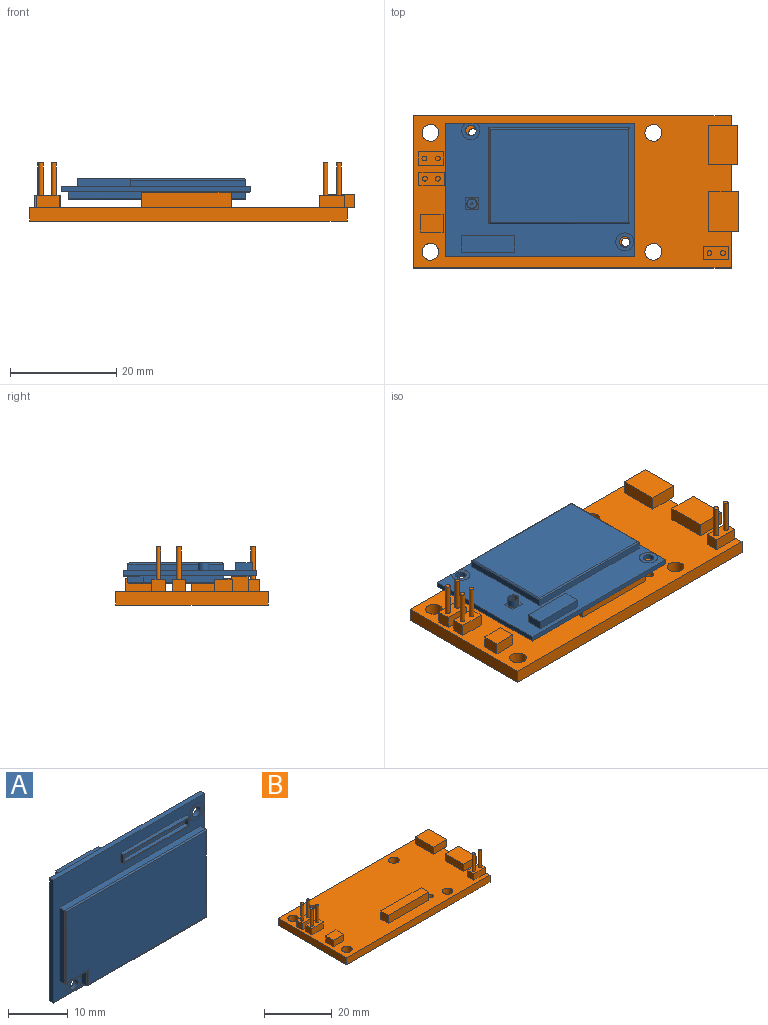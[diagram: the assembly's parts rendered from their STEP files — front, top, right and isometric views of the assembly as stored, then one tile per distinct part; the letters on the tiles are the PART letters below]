
ASSEMBLY  parts=2 mates=1
PART A: 64 faces, bbox 35.6x4x25.1 mm
  f0: plane 35.56x25.08mm, normal (0,1,0), area 359.8mm2, adj f2,f3,f4,f5,f6,f7,f8,f9
  f1: plane 35.56x25.08mm, normal (0,-1,0), area 260mm2, adj f2,f3,f4,f5,f11,f12,f13,f14
  f2: plane 25.08x0.95mm, normal (1,0,0), area 23.8mm2, adj f0,f1,f3,f5
  f3: plane 35.56x0.96mm, normal (0,0,-1), area 33.8mm2, adj f0,f1,f2,f4,f37,f38,f39,f40
  f4: plane 25.08x0.95mm, normal (-1,0,0), area 23.8mm2, adj f0,f1,f3,f5
  f5: plane 35.56x0.95mm, normal (0,0,1), area 33.8mm2, adj f0,f1,f2,f4
  f6: plane 18x1.25mm, normal (-1,0,0), area 22.5mm2, adj f0,f7,f9,f51
  f7: plane 26.5x1.25mm, normal (0,0,1), area 33.1mm2, adj f0,f6,f8,f49
  f8: plane 18x1.25mm, normal (1,0,0), area 22.5mm2, adj f0,f7,f9,f50
  f9: plane 26.5x1.25mm, normal (0,0,-1), area 33.1mm2, adj f0,f6,f8,f52
  f10: plane 26x17.5mm, normal (0,1,0), area 455mm2, adj f49,f50,f51,f52
  f11: plane 28.15x1.25mm, normal (0,0,-1), area 35.2mm2, adj f1,f12,f16,f47
  f12: plane 18x1.25mm, normal (1,0,0), area 22.5mm2, adj f1,f11,f13,f45
  f13: plane 33.4x1.25mm, normal (0,0,1), area 41.7mm2, adj f1,f12,f14,f43
  f14: plane 15x1.25mm, normal (-1,0,0), area 18.8mm2, adj f1,f13,f15,f44
  f15: plane 5.25x1.25mm, normal (0,0,-1), area 6.6mm2, adj f1,f14,f16,f46
  f16: plane 3x1.25mm, normal (-1,0,0), area 3.8mm2, adj f1,f11,f15,f48
  f17: plane 32.9x17.5mm, normal (0,-1,0), area 560mm2, adj f43,f44,f45,f46,f47,f48
  f18: plane 10x1.56mm, normal (0,0,-1), area 15.6mm2, adj f0,f19,f21,f22
  f19: plane 3.18x1.56mm, normal (-1,0,0), area 5mm2, adj f0,f18,f20,f22
  f20: plane 10x1.56mm, normal (0,0,1), area 15.6mm2, adj f0,f19,f21,f22
  f21: plane 3.18x1.56mm, normal (1,0,0), area 5mm2, adj f0,f18,f20,f22
  f22: plane 10x3.18mm, normal (0,1,0), area 31.8mm2, adj f18,f19,f20,f21
  f23: plane 15.5x1.85mm, normal (0,-1,0), area 8.4mm2, adj f24,f25,f26,f27,f28,f29,f30,f31
  f24: plane 15.5x0.75mm, normal (0,0,-1), area 11.6mm2, adj f1,f23,f25,f27
  f25: plane 1.85x0.75mm, normal (1,0,0), area 1.4mm2, adj f1,f23,f24,f26
  f26: plane 15.5x0.75mm, normal (0,0,1), area 11.6mm2, adj f1,f23,f25,f27
  f27: plane 1.85x0.75mm, normal (-1,0,0), area 1.4mm2, adj f1,f23,f24,f26
  f28: plane 1.35x0.75mm, normal (1,0,0), area 1mm2, adj f23,f29,f31,f32
  f29: plane 15x0.75mm, normal (0,0,1), area 11.2mm2, adj f23,f28,f30,f32
  f30: plane 1.35x0.75mm, normal (-1,0,0), area 1mm2, adj f23,f29,f31,f32
  f31: plane 15x0.75mm, normal (0,0,-1), area 11.2mm2, adj f23,f28,f30,f32
  f32: plane 15x1.35mm, normal (0,-1,0), area 20.3mm2, adj f28,f29,f30,f31
  f33: cylinder r=1mm len=2mm, axis (0,-1,0), area 6mm2, adj f35,f42
  f34: cylinder r=1mm len=2mm, axis (0,1,0), area 6mm2, adj f37,f40
  f35: plane 3.4x3.4mm, normal (0,1,0), area 5.9mm2, adj f33,f36
  f36: cylinder r=1.7mm len=3.4mm, axis (0,-1,0), area 0mm2, adj f0,f35
  f37: plane 3.4x3.06mm, normal (0,1,0), area 5.5mm2, adj f3,f34,f38
  f38: cylinder r=1.7mm len=3.4mm, axis (0,-1,0), area 0mm2, adj f0,f3,f37
  f39: cylinder r=1.7mm len=3.4mm, axis (0,-1,0), area 0mm2, adj f1,f3,f40
  f40: plane 3.4x3.06mm, normal (0,-1,0), area 5.5mm2, adj f3,f34,f39
  f41: cylinder r=1.7mm len=3.4mm, axis (0,-1,0), area 0mm2, adj f1,f42
  f42: plane 3.4x3.4mm, normal (0,-1,0), area 5.9mm2, adj f33,f41
  f43: cylinder r=0.25mm len=33.4mm, axis (1,0,0), area 13mm2, adj f13,f17,f44,f45
  f44: cylinder r=0.25mm len=15mm, axis (0,0,1), area 5.8mm2, adj f14,f17,f43,f46
  f45: cylinder r=0.25mm len=18mm, axis (0,0,-1), area 7mm2, adj f12,f17,f43,f47
  f46: cylinder r=0.25mm len=5.5mm, axis (-1,0,0), area 2.1mm2, adj f15,f17,f44,f48
  f47: cylinder r=0.25mm len=28.15mm, axis (-1,0,0), area 11mm2, adj f11,f17,f45,f48
  f48: cylinder r=0.25mm len=3.25mm, axis (0,0,1), area 1.2mm2, adj f16,f17,f46,f47
  f49: cylinder r=0.25mm len=26.5mm, axis (-1,0,0), area 10.3mm2, adj f7,f10,f50,f51
  f50: cylinder r=0.25mm len=18mm, axis (0,0,1), area 7mm2, adj f8,f10,f49,f52
  f51: cylinder r=0.25mm len=18mm, axis (0,0,-1), area 7mm2, adj f6,f10,f49,f52
  f52: cylinder r=0.25mm len=26.5mm, axis (1,0,0), area 10.3mm2, adj f9,f10,f50,f51
  f53: plane 2.49x2.22mm, normal (0,1,0), area 2.4mm2, adj f54,f55,f56,f57,f60
  f54: plane 2.22x0mm, normal (1,0,0), area 0mm2, adj f0,f53,f55,f57
  f55: plane 2.49x0mm, normal (0,0,-1), area 0mm2, adj f0,f53,f54,f56
  f56: plane 2.22x0mm, normal (-1,0,0), area 0mm2, adj f0,f53,f55,f57
  f57: plane 2.49x0mm, normal (0,0,1), area 0mm2, adj f0,f53,f54,f56
  f58: cylinder r=0.88mm len=1.75mm, axis (0,-1,0), area 8.2mm2, adj f59,f61
  f59: plane 2x2mm, normal (0,1,0), area 0.7mm2, adj f58,f60
  f60: cylinder r=1mm len=2mm, axis (0,-1,0), area 9.4mm2, adj f53,f59
  f61: plane 1.75x1.75mm, normal (0,1,0), area 2.3mm2, adj f58,f63
  f62: plane 0.4x0.4mm, normal (0,1,0), area 0.1mm2, adj f63
  f63: cylinder r=0.2mm len=1.5mm, axis (0,-1,0), area 1.9mm2, adj f61,f62
PART B: 61 faces, bbox 61.1x28.6x10.9 mm
  f0: plane 59.69x2.54mm, normal (0,-1,0), area 151.6mm2, adj f1,f9,f10,f11
  f1: plane 28.58x2.54mm, normal (1,0,0), area 72.6mm2, adj f0,f2,f10,f11,f12,f18
  f2: plane 59.69x2.54mm, normal (0,1,0), area 151.6mm2, adj f1,f9,f10,f11
  f3: cylinder r=1.57mm len=3.15mm, axis (0,0,-1), area 25.1mm2, adj f10,f11
  f4: cylinder r=1.57mm len=3.15mm, axis (0,0,-1), area 25.1mm2, adj f10,f11
  f5: cylinder r=1.57mm len=3.15mm, axis (0,0,-1), area 25.1mm2, adj f10,f11
  f6: cylinder r=1.57mm len=3.15mm, axis (0,0,-1), area 25.1mm2, adj f10,f11
  f7: cylinder r=0.79mm len=2.54mm, axis (0,0,-1), area 12.7mm2, adj f10,f11
  f8: cylinder r=0.79mm len=2.54mm, axis (0,0,-1), area 12.7mm2, adj f10,f11
  f9: plane 28.58x2.54mm, normal (-1,0,0), area 72.6mm2, adj f0,f2,f10,f11
  f10: plane 59.69x28.58mm, normal (0,0,1), area 1504mm2, adj f0,f1,f2,f3,f4,f5,f6,f7
  f11: plane 59.69x28.58mm, normal (0,0,-1), area 1670.5mm2, adj f0,f1,f2,f3,f4,f5,f6,f7
  f12: plane 7.5x1.28mm, normal (0,0,-1), area 9.6mm2, adj f1,f14,f15,f16
  f13: plane 7.5x2.54mm, normal (-1,0,0), area 19.1mm2, adj f10,f14,f16,f17
  f14: plane 5.6x2.54mm, normal (0,-1,0), area 14.2mm2, adj f10,f12,f13,f15,f17
  f15: plane 7.5x2.54mm, normal (1,0,0), area 19.1mm2, adj f12,f14,f16,f17
  f16: plane 5.6x2.54mm, normal (0,1,0), area 14.2mm2, adj f10,f12,f13,f15,f17
  f17: plane 7.5x5.6mm, normal (0,0,1), area 42mm2, adj f13,f14,f15,f16
  f18: plane 7.5x1.4mm, normal (0,0,-1), area 10.5mm2, adj f1,f19,f21,f22
  f19: plane 5.6x2.54mm, normal (0,1,0), area 14.2mm2, adj f10,f18,f20,f22,f23
  f20: plane 7.5x2.54mm, normal (-1,0,0), area 19.1mm2, adj f10,f19,f21,f23
  f21: plane 5.6x2.54mm, normal (0,-1,0), area 14.2mm2, adj f10,f18,f20,f22,f23
  f22: plane 7.5x2.54mm, normal (1,0,0), area 19.1mm2, adj f18,f19,f21,f23
  f23: plane 7.5x5.6mm, normal (0,0,1), area 42mm2, adj f19,f20,f21,f22
  f24: plane 3.14x2.92mm, normal (-1,0,0), area 9.2mm2, adj f10,f25,f27,f28
  f25: plane 16.8x2.92mm, normal (0,-1,0), area 49.1mm2, adj f10,f24,f26,f28
  f26: plane 3.14x2.92mm, normal (1,0,0), area 9.2mm2, adj f10,f25,f27,f28
  f27: plane 16.8x2.92mm, normal (0,1,0), area 49.1mm2, adj f10,f24,f26,f28
  f28: plane 16.8x3.14mm, normal (0,0,1), area 52.8mm2, adj f24,f25,f26,f27
  f29: plane 2.49x2.29mm, normal (1,0,0), area 5.7mm2, adj f10,f30,f32,f33
  f30: plane 4.83x2.29mm, normal (0,1,0), area 11mm2, adj f10,f29,f31,f33
  f31: plane 2.49x2.29mm, normal (-1,0,0), area 5.7mm2, adj f10,f30,f32,f33
  f32: plane 4.83x2.29mm, normal (0,-1,0), area 11mm2, adj f10,f29,f31,f33
  f33: plane 4.83x2.49mm, normal (0,0,1), area 10.8mm2, adj f29,f30,f31,f32,f57,f59
  f34: plane 2.49x2.29mm, normal (-1,0,0), area 5.7mm2, adj f10,f35,f37,f38
  f35: plane 4.83x2.29mm, normal (0,-1,0), area 11mm2, adj f10,f34,f36,f38
  f36: plane 2.49x2.29mm, normal (1,0,0), area 5.7mm2, adj f10,f35,f37,f38
  f37: plane 4.83x2.29mm, normal (0,1,0), area 11mm2, adj f10,f34,f36,f38
  f38: plane 4.83x2.49mm, normal (0,0,1), area 10.8mm2, adj f34,f35,f36,f37,f49,f51
  f39: plane 4.83x2.29mm, normal (0,-1,0), area 11mm2, adj f10,f40,f42,f43
  f40: plane 2.49x2.29mm, normal (1,0,0), area 5.7mm2, adj f10,f39,f41,f43
  f41: plane 4.83x2.29mm, normal (0,1,0), area 11mm2, adj f10,f40,f42,f43
  f42: plane 2.49x2.29mm, normal (-1,0,0), area 5.7mm2, adj f10,f39,f41,f43
  f43: plane 4.83x2.49mm, normal (0,0,1), area 10.8mm2, adj f39,f40,f41,f42,f53,f55
  f44: plane 3.25x2.29mm, normal (-1,0,0), area 7.4mm2, adj f10,f45,f47,f48
  f45: plane 4.24x2.29mm, normal (0,-1,0), area 9.7mm2, adj f10,f44,f46,f48
  f46: plane 3.25x2.29mm, normal (1,0,0), area 7.4mm2, adj f10,f45,f47,f48
  f47: plane 4.24x2.29mm, normal (0,1,0), area 9.7mm2, adj f10,f44,f46,f48
  f48: plane 4.24x3.25mm, normal (0,0,1), area 13.8mm2, adj f44,f45,f46,f47
  f49: cylinder r=0.44mm len=6.1mm, axis (0,0,-1), area 17mm2, adj f38,f50
  f50: plane 0.89x0.89mm, normal (0,0,1), area 0.6mm2, adj f49
  f51: cylinder r=0.44mm len=6.1mm, axis (0,0,-1), area 17mm2, adj f38,f52
  f52: plane 0.89x0.89mm, normal (0,0,1), area 0.6mm2, adj f51
  f53: cylinder r=0.44mm len=6.1mm, axis (0,0,-1), area 17mm2, adj f43,f54
  f54: plane 0.89x0.89mm, normal (0,0,1), area 0.6mm2, adj f53
  f55: cylinder r=0.44mm len=6.1mm, axis (0,0,-1), area 17mm2, adj f43,f56
  f56: plane 0.89x0.89mm, normal (0,0,1), area 0.6mm2, adj f55
  f57: cylinder r=0.44mm len=6.1mm, axis (0,0,-1), area 17mm2, adj f33,f58
  f58: plane 0.89x0.89mm, normal (0,0,1), area 0.6mm2, adj f57
  f59: cylinder r=0.44mm len=6.1mm, axis (0,0,-1), area 17mm2, adj f33,f60
  f60: plane 0.89x0.89mm, normal (0,0,1), area 0.6mm2, adj f59
PLACE A rot(axis=(1,0,0),90deg) t=(-9.33,21.24,33.82)mm
PLACE B t=(-2.54,20.89,28.36)mm
MATE fastened B.f28 <-> A.f32  axis (0,0,1) through (-3.6,11.93,33.82)mm
